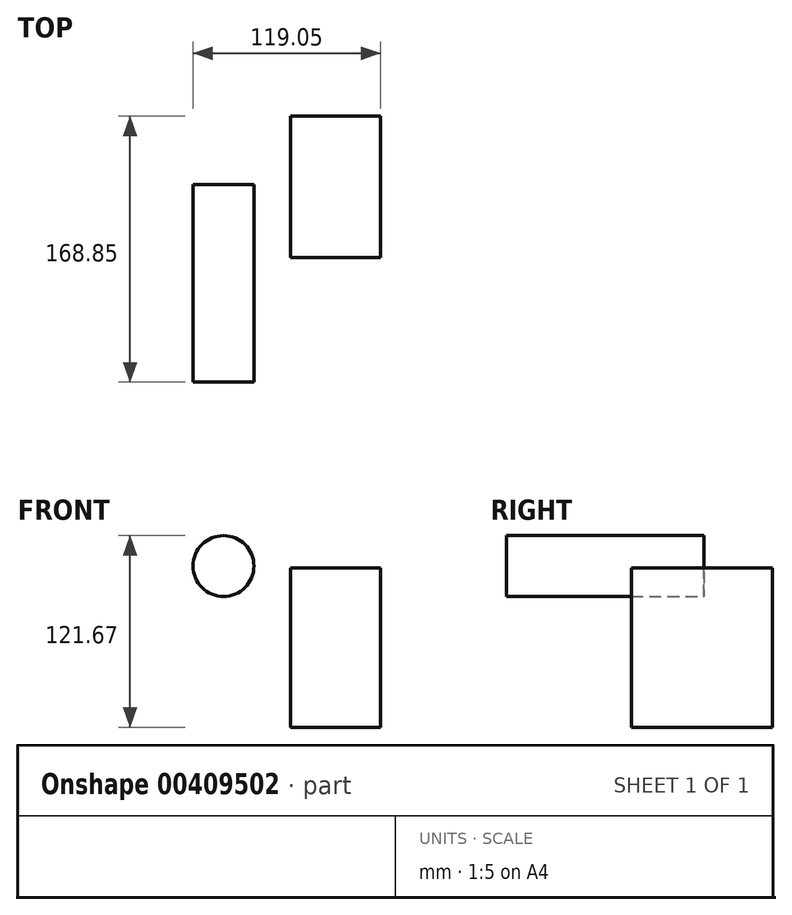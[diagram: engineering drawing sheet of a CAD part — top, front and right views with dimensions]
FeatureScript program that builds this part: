
annotation { "Feature Type Name" : "Feature", "Feature Type Description" : "" }
export const myFeature = defineFeature(function(context is Context, id is Id, definition is map)
    precondition{}
    {
        {
            var Q0;
            Q0=qCreatedBy(makeId("Right.planeOp"),FACE);
            var sketch = newSketch(context, id + "F0", { "sketchPlane" : qUnion([Q0])});
            skLineSegment(sketch, "E0.bottom", {"start": v(-46.25, 56.18) * mm, "end": v(43.37, 56.18) * mm});
            skLineSegment(sketch, "E0.top", {"start": v(-46.25, -44.9) * mm, "end": v(43.37, -44.9) * mm});
            skLineSegment(sketch, "E0.left", {"start": v(-46.25, 56.18) * mm, "end": v(-46.25, -44.9) * mm});
            skLineSegment(sketch, "E0.right", {"start": v(43.37, 56.18) * mm, "end": v(43.37, -44.9) * mm});
            skSolve(sketch);
        }
        {
            var Q0;
            Q0 = qSketchRegion(id + "F0", true);
            extrude(context, id + "F1", {"entities" : qUnion([Q0]), "depth" : 57.15 * mm, "offsetDistance" : 25.4 * mm});
        }
        {
            var Q0;
            Q0=qCreatedBy(makeId("Front.planeOp"),FACE);
            var sketch = newSketch(context, id + "F2", { "sketchPlane" : qUnion([Q0])});
            skCircle(sketch, "E1", {"center": v(-42.58, 57.46) * mm, "radius": 19.32 * mm});
            skSolve(sketch);
        }
        {
            var Q0;
            Q0 = qSketchRegion(id + "F2", true);
            extrude(context, id + "F3", {"entities" : qUnion([Q0]), "depth" : 125.48 * mm, "offsetDistance" : 25.4 * mm});
        }
    });
